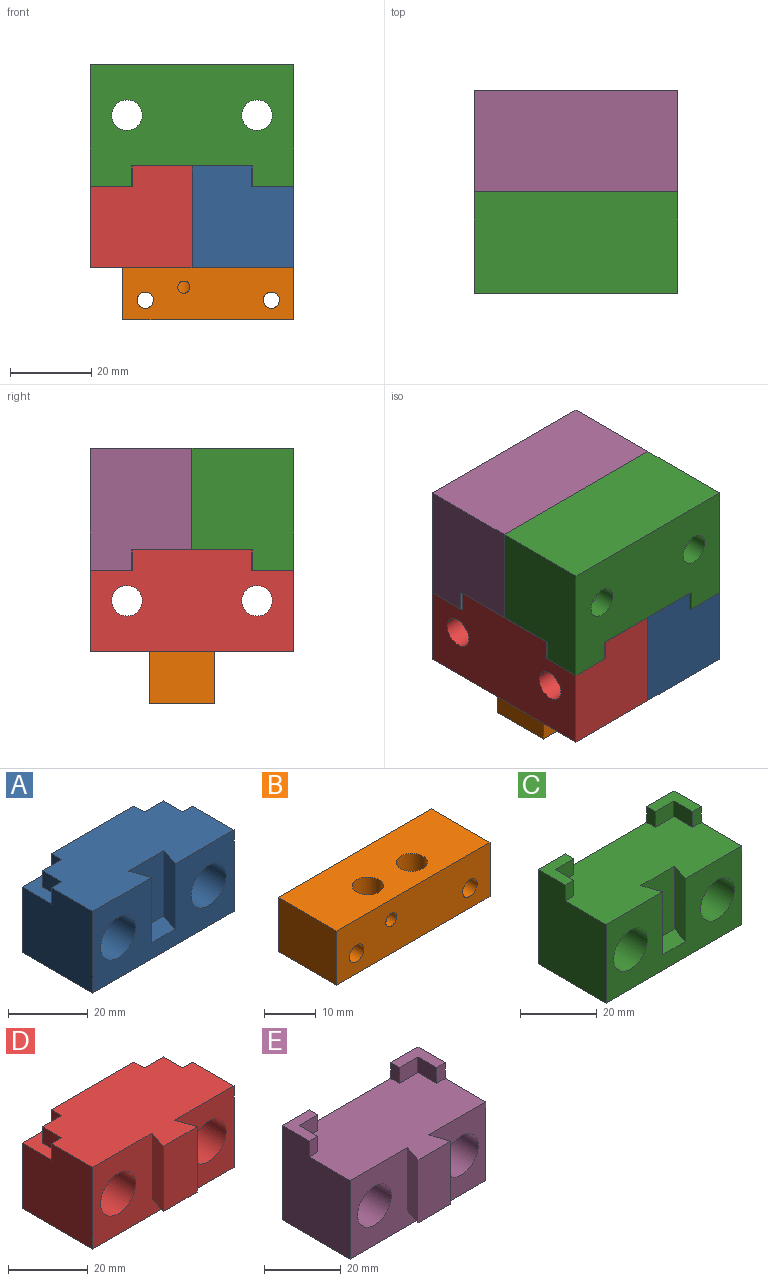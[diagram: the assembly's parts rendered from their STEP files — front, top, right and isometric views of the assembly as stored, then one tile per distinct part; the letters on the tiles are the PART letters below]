
ASSEMBLY  parts=5 mates=11
PART A: 26 faces, bbox 50x25x25 mm
  f0: plane 25x25mm, normal (1,0,0), area 573mm2, adj f2,f3,f4,f5,f17,f20
  f1: plane 25x25mm, normal (-1,0,0), area 573mm2, adj f2,f3,f4,f5,f22,f25
  f2: plane 50x25mm, normal (0,1,0), area 1057.6mm2, adj f0,f1,f3,f5,f8,f10,f18,f20
  f3: plane 50x25mm, normal (0,0,1), area 1063.8mm2, adj f0,f1,f2,f4,f12,f13,f14,f16
  f4: plane 50x25mm, normal (0,-1,0), area 840.5mm2, adj f0,f1,f3,f5,f6,f7,f12,f13
  f5: plane 50x25mm, normal (0,0,-1), area 1250mm2, adj f0,f1,f2,f4
  f6: cylinder r=6.2mm len=20mm, axis (0,1,0), area 779.1mm2, adj f4,f9
  f7: cylinder r=6.2mm len=20mm, axis (0,1,0), area 779.1mm2, adj f4,f11
  f8: cylinder r=3.75mm len=7.5mm, axis (0,1,0), area 117.8mm2, adj f2,f9
  f9: plane 12.4x12.4mm, normal (0,-1,0), area 76.6mm2, adj f6,f8
  f10: cylinder r=3.75mm len=7.5mm, axis (0,1,0), area 117.8mm2, adj f2,f11
  f11: plane 12.4x12.4mm, normal (0,-1,0), area 76.6mm2, adj f7,f10
  f12: plane 20x6mm, normal (0.95,0.32,0), area 126.5mm2, adj f3,f4,f14,f15
  f13: plane 20x6mm, normal (-0.95,0.32,0), area 126.5mm2, adj f3,f4,f14,f15
  f14: plane 20x12.4mm, normal (0,-1,0), area 248mm2, adj f3,f12,f13,f15
  f15: plane 12.4x6mm, normal (0,0,1), area 62.4mm2, adj f4,f12,f13,f14
  f16: plane 6.8x5mm, normal (1,0,0), area 34mm2, adj f3,f17,f19,f20
  f17: plane 5x3.6mm, normal (0,1,0), area 18mm2, adj f0,f3,f16,f20
  f18: plane 5x3.6mm, normal (1,0,0), area 18mm2, adj f2,f3,f19,f20
  f19: plane 6.8x5mm, normal (0,1,0), area 34mm2, adj f3,f16,f18,f20
  f20: plane 10.4x10.4mm, normal (0,0,1), area 61.9mm2, adj f0,f2,f16,f17,f18,f19
  f21: plane 5x3.6mm, normal (-1,0,0), area 18mm2, adj f2,f3,f24,f25
  f22: plane 5x3.6mm, normal (0,1,0), area 18mm2, adj f1,f3,f23,f25
  f23: plane 6.8x5mm, normal (-1,0,0), area 34mm2, adj f3,f22,f24,f25
  f24: plane 6.8x5mm, normal (0,1,0), area 34mm2, adj f3,f21,f23,f25
  f25: plane 10.4x10.4mm, normal (0,0,1), area 61.9mm2, adj f1,f2,f21,f22,f23,f24
PART B: 11 faces, bbox 42x16x12.8 mm
  f0: plane 16x12.8mm, normal (1,0,0), area 204.8mm2, adj f1,f4,f6,f7
  f1: plane 42x16mm, normal (0,0,1), area 615.5mm2, adj f0,f2,f6,f7,f8,f9
  f2: plane 16x12.8mm, normal (-1,0,0), area 204.8mm2, adj f1,f4,f6,f7
  f3: cylinder r=2mm len=16mm, axis (0,1,0), area 201.1mm2, adj f6,f7
  f4: plane 42x16mm, normal (0,0,-1), area 615.5mm2, adj f0,f2,f6,f7,f8,f9
  f5: cylinder r=2mm len=16mm, axis (0,1,0), area 201.1mm2, adj f6,f7
  f6: plane 42x12.8mm, normal (0,-1,0), area 505.4mm2, adj f0,f1,f2,f3,f4,f5,f10
  f7: plane 42x12.8mm, normal (0,1,0), area 512.5mm2, adj f0,f1,f2,f3,f4,f5
  f8: cylinder r=3mm len=12.8mm, axis (0,0,1), area 241.3mm2, adj f1,f4
  f9: cylinder r=3mm len=12.8mm, axis (0,0,1), area 234mm2, adj f1,f4,f10
  f10: cylinder r=1.5mm len=3.8mm, axis (0,-1,0), area 33.9mm2, adj f6,f9
PART C: 26 faces, bbox 50x25x30 mm
  f0: plane 50x25mm, normal (0,0,1), area 1080.1mm2, adj f1,f3,f6,f7,f12,f13,f14,f16
  f1: plane 50x25mm, normal (0,-1,0), area 840.5mm2, adj f0,f2,f3,f4,f5,f6,f12,f13
  f2: plane 50x25mm, normal (0,0,-1), area 1250mm2, adj f1,f3,f6,f7
  f3: plane 30x25mm, normal (1,0,0), area 675mm2, adj f0,f1,f2,f7,f22,f25
  f4: cylinder r=6.2mm len=20mm, axis (0,1,0), area 779.1mm2, adj f1,f9
  f5: cylinder r=6.2mm len=20mm, axis (0,1,0), area 779.1mm2, adj f1,f11
  f6: plane 30x25mm, normal (-1,0,0), area 675mm2, adj f0,f1,f2,f7,f17,f20
  f7: plane 50x30mm, normal (0,1,0), area 1261.6mm2, adj f0,f2,f3,f6,f8,f10,f16,f20
  f8: cylinder r=3.75mm len=7.5mm, axis (0,1,0), area 117.8mm2, adj f7,f9
  f9: plane 12.4x12.4mm, normal (0,-1,0), area 76.6mm2, adj f4,f8
  f10: cylinder r=3.75mm len=7.5mm, axis (0,1,0), area 117.8mm2, adj f7,f11
  f11: plane 12.4x12.4mm, normal (0,-1,0), area 76.6mm2, adj f5,f10
  f12: plane 20x6mm, normal (0.95,0.32,0), area 126.5mm2, adj f0,f1,f14,f15
  f13: plane 20x6mm, normal (-0.95,0.32,0), area 126.5mm2, adj f0,f1,f14,f15
  f14: plane 20x12.4mm, normal (0,-1,0), area 248mm2, adj f0,f12,f13,f15
  f15: plane 12.4x6mm, normal (0,0,1), area 62.4mm2, adj f1,f12,f13,f14
  f16: plane 5x3.2mm, normal (1,0,0), area 16mm2, adj f0,f7,f19,f20
  f17: plane 5x3.2mm, normal (0,-1,0), area 16mm2, adj f0,f6,f18,f20
  f18: plane 6.8x5mm, normal (1,0,0), area 34mm2, adj f0,f17,f19,f20
  f19: plane 6.8x5mm, normal (0,-1,0), area 34mm2, adj f0,f16,f18,f20
  f20: plane 10x10mm, normal (0,0,1), area 53.8mm2, adj f6,f7,f16,f17,f18,f19
  f21: plane 6.8x5mm, normal (-1,0,0), area 34mm2, adj f0,f22,f24,f25
  f22: plane 5x3.2mm, normal (0,-1,0), area 16mm2, adj f0,f3,f21,f25
  f23: plane 5x3.2mm, normal (-1,0,0), area 16mm2, adj f0,f7,f24,f25
  f24: plane 6.8x5mm, normal (0,-1,0), area 34mm2, adj f0,f21,f23,f25
  f25: plane 10x10mm, normal (0,0,1), area 53.8mm2, adj f3,f7,f21,f22,f23,f24
PART D: 26 faces, bbox 50x31x25 mm
  f0: plane 25x25mm, normal (1,0,0), area 573mm2, adj f2,f3,f4,f7,f19,f20
  f1: plane 25x25mm, normal (-1,0,0), area 573mm2, adj f2,f3,f4,f7,f22,f25
  f2: plane 50x25mm, normal (0,1,0), area 1057.6mm2, adj f0,f1,f3,f4,f8,f10,f16,f20
  f3: plane 50x31mm, normal (0,0,1), area 1186.2mm2, adj f0,f1,f2,f7,f12,f13,f14,f16
  f4: plane 50x25mm, normal (0,0,-1), area 1250mm2, adj f0,f1,f2,f7
  f5: cylinder r=6.2mm len=20mm, axis (0,1,0), area 779.1mm2, adj f7,f9
  f6: cylinder r=6.2mm len=20mm, axis (0,1,0), area 779.1mm2, adj f7,f11
  f7: plane 50x25mm, normal (0,-1,0), area 848.5mm2, adj f0,f1,f3,f4,f5,f6,f12,f14
  f8: cylinder r=3.75mm len=7.5mm, axis (0,1,0), area 117.8mm2, adj f2,f9
  f9: plane 12.4x12.4mm, normal (0,-1,0), area 76.6mm2, adj f5,f8
  f10: cylinder r=3.75mm len=7.5mm, axis (0,1,0), area 117.8mm2, adj f2,f11
  f11: plane 12.4x12.4mm, normal (0,-1,0), area 76.6mm2, adj f6,f10
  f12: plane 20x6mm, normal (-0.95,0.32,0), area 126.5mm2, adj f3,f7,f13,f15
  f13: plane 20x12mm, normal (0,-1,0), area 240mm2, adj f3,f12,f14,f15
  f14: plane 20x6mm, normal (0.95,0.32,0), area 126.5mm2, adj f3,f7,f13,f15
  f15: plane 12x6mm, normal (0,0,-1), area 60mm2, adj f7,f12,f13,f14
  f16: plane 5x3.6mm, normal (1,0,0), area 18mm2, adj f2,f3,f17,f20
  f17: plane 6.8x5mm, normal (0,1,0), area 34mm2, adj f3,f16,f18,f20
  f18: plane 6.8x5mm, normal (1,0,0), area 34mm2, adj f3,f17,f19,f20
  f19: plane 5x3.6mm, normal (0,1,0), area 18mm2, adj f0,f3,f18,f20
  f20: plane 10.4x10.4mm, normal (0,0,1), area 61.9mm2, adj f0,f2,f16,f17,f18,f19
  f21: plane 5x3.6mm, normal (-1,0,0), area 18mm2, adj f2,f3,f24,f25
  f22: plane 5x3.6mm, normal (0,1,0), area 18mm2, adj f1,f3,f23,f25
  f23: plane 6.8x5mm, normal (-1,0,0), area 34mm2, adj f3,f22,f24,f25
  f24: plane 6.8x5mm, normal (0,1,0), area 34mm2, adj f3,f21,f23,f25
  f25: plane 10.4x10.4mm, normal (0,0,1), area 61.9mm2, adj f1,f2,f21,f22,f23,f24
PART E: 26 faces, bbox 50x31x30 mm
  f0: plane 50x31mm, normal (0,0,1), area 1202.5mm2, adj f2,f5,f6,f7,f12,f13,f14,f16
  f1: plane 50x25mm, normal (0,0,-1), area 1250mm2, adj f2,f5,f6,f7
  f2: plane 30x25mm, normal (1,0,0), area 675mm2, adj f0,f1,f6,f7,f24,f25
  f3: cylinder r=6.2mm len=20mm, axis (0,1,0), area 779.1mm2, adj f6,f9
  f4: cylinder r=6.2mm len=20mm, axis (0,1,0), area 779.1mm2, adj f6,f11
  f5: plane 30x25mm, normal (-1,0,0), area 675mm2, adj f0,f1,f6,f7,f17,f20
  f6: plane 50x25mm, normal (0,-1,0), area 848.5mm2, adj f0,f1,f2,f3,f4,f5,f12,f14
  f7: plane 50x30mm, normal (0,1,0), area 1261.6mm2, adj f0,f1,f2,f5,f8,f10,f16,f20
  f8: cylinder r=3.75mm len=7.5mm, axis (0,1,0), area 117.8mm2, adj f7,f9
  f9: plane 12.4x12.4mm, normal (0,-1,0), area 76.6mm2, adj f3,f8
  f10: cylinder r=3.75mm len=7.5mm, axis (0,1,0), area 117.8mm2, adj f7,f11
  f11: plane 12.4x12.4mm, normal (0,-1,0), area 76.6mm2, adj f4,f10
  f12: plane 20x6mm, normal (-0.95,0.32,0), area 126.5mm2, adj f0,f6,f13,f15
  f13: plane 20x12mm, normal (0,-1,0), area 240mm2, adj f0,f12,f14,f15
  f14: plane 20x6mm, normal (0.95,0.32,0), area 126.5mm2, adj f0,f6,f13,f15
  f15: plane 12x6mm, normal (0,0,-1), area 60mm2, adj f6,f12,f13,f14
  f16: plane 5x3.2mm, normal (1,0,0), area 16mm2, adj f0,f7,f19,f20
  f17: plane 5x3.2mm, normal (0,-1,0), area 16mm2, adj f0,f5,f18,f20
  f18: plane 6.8x5mm, normal (1,0,0), area 34mm2, adj f0,f17,f19,f20
  f19: plane 6.8x5mm, normal (0,-1,0), area 34mm2, adj f0,f16,f18,f20
  f20: plane 10x10mm, normal (0,0,1), area 53.8mm2, adj f5,f7,f16,f17,f18,f19
  f21: plane 5x3.2mm, normal (-1,0,0), area 16mm2, adj f0,f7,f22,f25
  f22: plane 6.8x5mm, normal (0,-1,0), area 34mm2, adj f0,f21,f23,f25
  f23: plane 6.8x5mm, normal (-1,0,0), area 34mm2, adj f0,f22,f24,f25
  f24: plane 5x3.2mm, normal (0,-1,0), area 16mm2, adj f0,f2,f23,f25
  f25: plane 10x10mm, normal (0,0,1), area 53.8mm2, adj f2,f7,f21,f22,f23,f24
PLACE A rot(axis=(0,0,-1),90deg) t=(25.56,0.69,-5.97)mm fixed
PLACE B rot(axis=(0.1,0.05,-0.99),0deg) t=(4.56,11.08,-26.47)mm
PLACE C rot(axis=(1,0,0),180deg) t=(0.56,-24.31,19.03)mm
PLACE D rot(axis=(0,0,1),90deg) t=(-24.44,0.69,-5.97)mm
PLACE E rot(axis=(0,1,0),180deg) t=(0.56,25.69,19.03)mm
MATE planar A.f5 <-> B.f8  axis (0,0,-1) through (13.06,0.69,-18.47)mm
MATE cylindrical A.f6 <-> D.f10  axis (1,0,0) through (10.56,16.69,-5.97)mm
MATE planar E.f13 <-> C.f14  axis (0,-1,0) through (0.56,-5.31,16.53)mm
MATE planar D.f2 <-> E.f2  axis (-1,0,0) through (-24.44,0.69,-6.95)mm
MATE planar A.f3 <-> D.f3  axis (0,0,1) through (12.6,0.69,6.53)mm
MATE planar E.f0 <-> D.f3  axis (0,0,-1) through (0.56,11.61,6.53)mm
MATE cylindrical E.f3 <-> C.f10  axis (0,1,0) through (16.56,10.69,19.03)mm
MATE planar D.f1 <-> C.f7  axis (0,-1,0) through (-11.27,-24.31,-6.87)mm
MATE planar A.f14 <-> D.f13  axis (-1,0,0) through (6.56,0.69,-3.47)mm
MATE planar C.f0 <-> E.f0  axis (0,0,-1) through (0.56,-11.47,6.53)mm
MATE planar A.f2 <-> B.f0  axis (1,0,0) through (25.56,0.69,-6.95)mm
